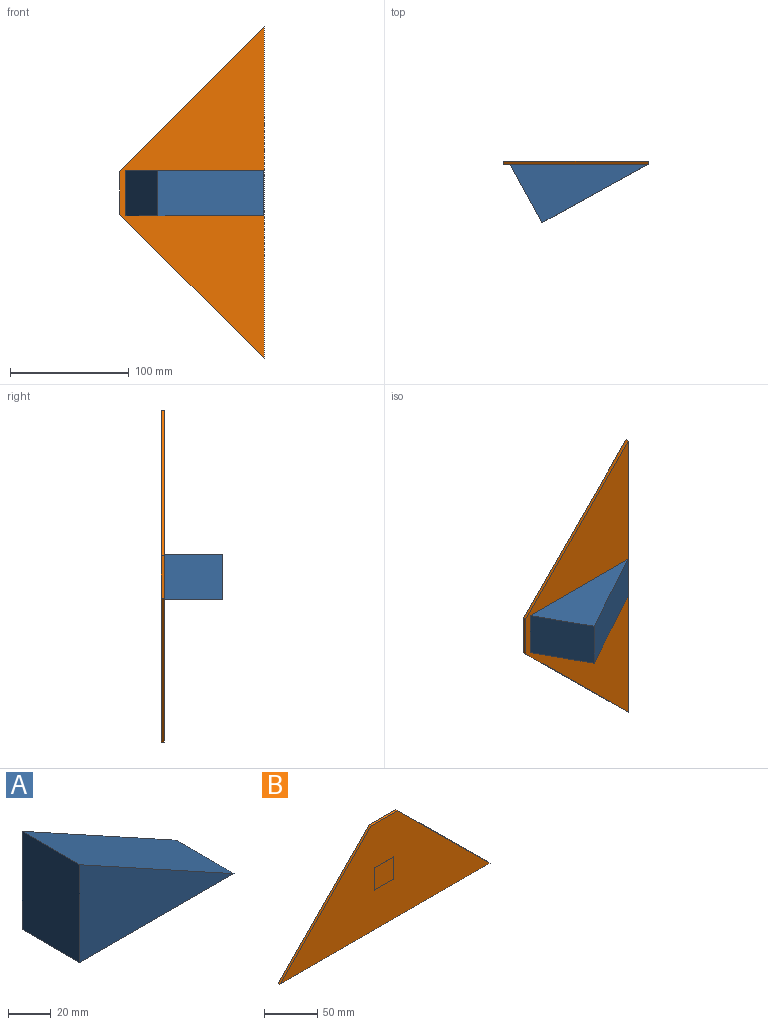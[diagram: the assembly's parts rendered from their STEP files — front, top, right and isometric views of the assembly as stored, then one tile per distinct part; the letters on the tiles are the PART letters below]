
ASSEMBLY  parts=2 mates=1
PART A: 5 faces, bbox 101.6x38.1x55.9 mm
  f0: plane 55.88x38.1mm, normal (-1,0,0), area 2129mm2, adj f1,f2,f3,f4
  f1: plane 101.6x38.1mm, normal (0,0,-1), area 3871mm2, adj f0,f2,f3,f4
  f2: plane 101.6x55.88mm, normal (0.48,0,0.88), area 4417.8mm2, adj f0,f1,f3,f4
  f3: plane 101.6x55.88mm, normal (0,-1,0), area 2838.7mm2, adj f0,f1,f2
  f4: plane 101.6x55.88mm, normal (0,1,0), area 2838.7mm2, adj f0,f1,f2
PART B: 11 faces, bbox 279.4x2.6x121.6 mm
  f0: plane 36.14x2.54mm, normal (0,0,1), area 91.8mm2, adj f1,f3,f4,f5
  f1: plane 121.63x120.75mm, normal (-0.71,0,0.7), area 435.3mm2, adj f0,f2,f4,f5
  f2: plane 279.4x2.54mm, normal (0,0,-1), area 709.7mm2, adj f1,f3,f4,f5
  f3: plane 122.51x121.63mm, normal (0.7,0,0.71), area 438.5mm2, adj f0,f2,f4,f5
  f4: plane 279.4x121.63mm, normal (0,-1,0), area 18543.9mm2, adj f0,f1,f2,f3,f6,f7,f8,f9
  f5: plane 279.4x121.63mm, normal (0,1,0), area 19189mm2, adj f0,f1,f2,f3
  f6: plane 25.4x0.03mm, normal (1,0,0), area 0.6mm2, adj f4,f7,f9,f10
  f7: plane 25.4x0.03mm, normal (0,0,1), area 0.6mm2, adj f4,f6,f8,f10
  f8: plane 25.4x0.03mm, normal (-1,0,0), area 0.6mm2, adj f4,f7,f9,f10
  f9: plane 25.4x0.03mm, normal (0,0,-1), area 0.6mm2, adj f4,f6,f8,f10
  f10: plane 25.4x25.4mm, normal (0,-1,0), area 645.2mm2, adj f6,f7,f8,f9
PLACE A rot(axis=(-0.94,-0.24,0.24),93.5deg) t=(7.41,-2.54,13.76)mm
PLACE B rot(axis=(0,-1,0),90deg) t=(65.83,0.03,32.81)mm
MATE fastened B.f10 <-> A.f2  axis (0,-1,0) through (7.41,-2.54,32.81)mm
